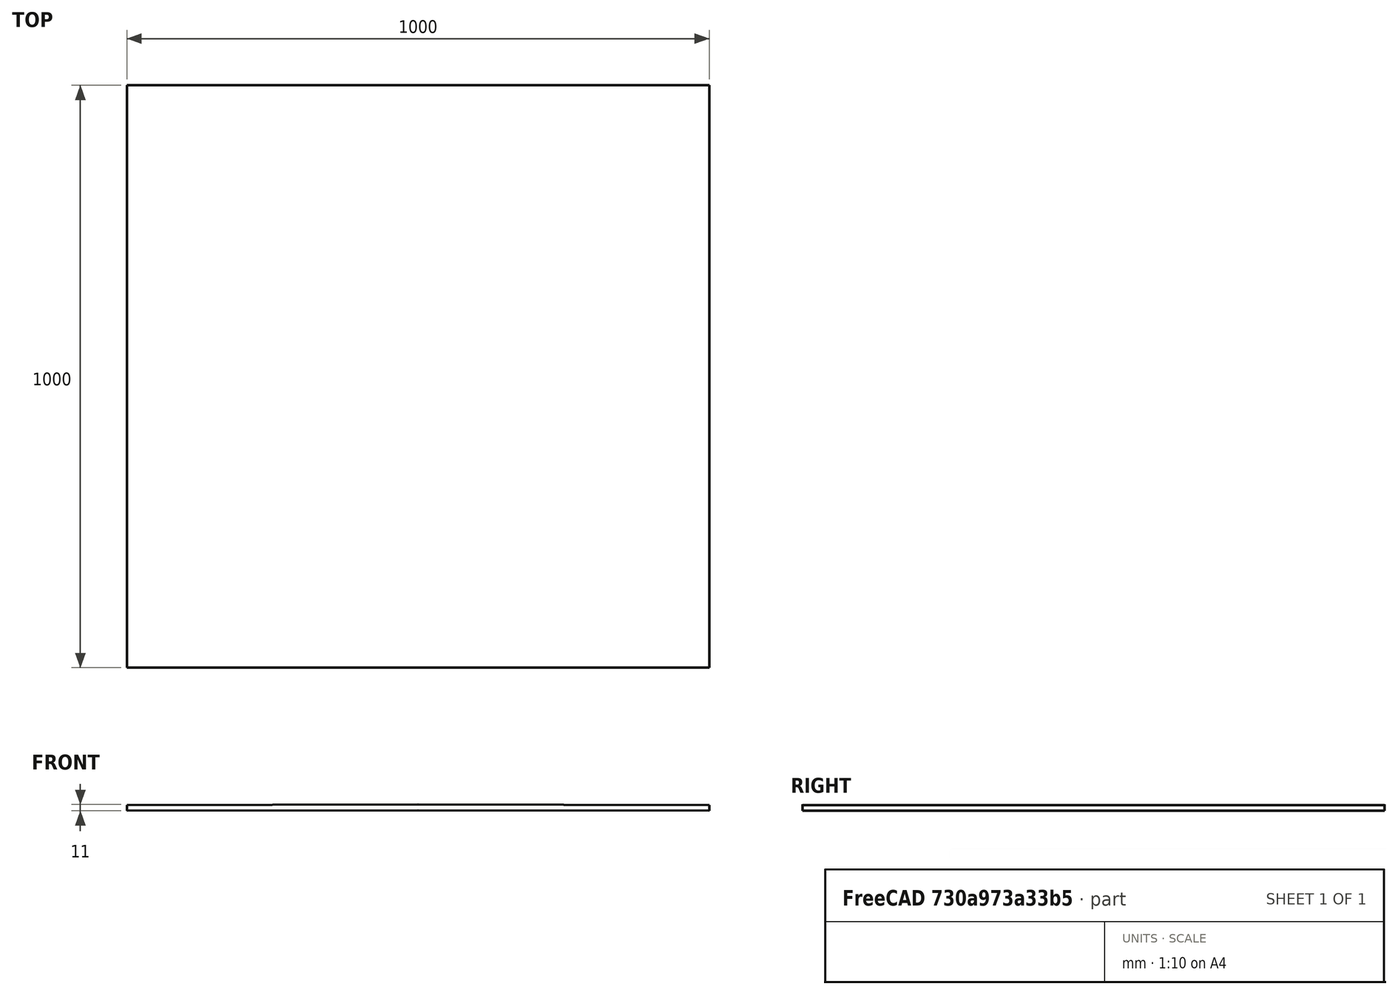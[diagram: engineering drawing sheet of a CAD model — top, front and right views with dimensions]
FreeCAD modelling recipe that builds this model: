
FCSTD DOCUMENT  (FreeCAD 0.21R33694 (Git))
Label: Elastica_3
License: All rights reserved
LicenseURL: http://en.wikipedia.org/wiki/All_rights_reserved
objects: Fem::ConstraintDisplacement×3, Sketcher::SketchObject×1, Part::Extrusion×1, App::MaterialObjectPython×1, Fem::ConstraintFixed×1, Fem::ConstraintForce×1, Fem::FemMeshObjectPython×1, Fem::FemSolverObjectPython×1, Fem::FemAnalysis×1
note: 2 computed .brp shape members not serialized (recipe doc carries the construction recipe); baked Part::Feature solids carry a one-line shape summary decoded from their .brp

FEATURE [Sketcher::SketchObject] Sketch
  FullyConstrained = true
  Placement = pos=(0,0,0) rot=(1,0,0;1.5708rad)
  sketch-geometry (6):
    g0: LineSegment StartX=0 StartY=0 StartZ=0 EndX=0 EndY=10 EndZ=0
    g1: LineSegment StartX=0 StartY=10 StartZ=0 EndX=500 EndY=11 EndZ=0
    g2: LineSegment StartX=500 StartY=11 StartZ=0 EndX=1000 EndY=10 EndZ=0
    g3: LineSegment StartX=1000 StartY=10 StartZ=0 EndX=1000 EndY=0 EndZ=0
    g4: LineSegment StartX=1000 StartY=0 StartZ=0 EndX=500 EndY=1 EndZ=0
    g5: LineSegment StartX=500 StartY=1 StartZ=0 EndX=0 EndY=-1e-16 EndZ=0
  constraints (17):
    c: Coincident(g-1,g0)
    c: PointOnObject(g0,g-2)
    c: Coincident(g0,g1)
    c: Coincident(g1,g2)
    c: Coincident(g2,g3)
    c: Vertical(g3)
    c: Coincident(g3,g4)
    c: Coincident(g4,g5)
    c: Coincident(g5,g0)
    c: DistanceY(g0,g0) = 10
    c: DistanceY(g3,g3) = 10
    c: DistanceY(g4,g1) = 10
    c: PointOnObject(g3,g-1)
    c: DistanceX(g0,g3) = 1000
    c: DistanceY(g0,g4) = 1
    c: DistanceX(g0,g4) = 500
    c: DistanceX(g0,g1) = 500
FEATURE [Part::Extrusion] Extrude
  Base = -> Sketch
  Dir = (0,-1,2e-16)
  DirMode = 2
  FaceMakerClass = Part::FaceMakerBullseye
  LengthFwd = 0
  LengthRev = 1000
  Solid = true
  Symmetric = false
FEATURE [App::MaterialObjectPython] MaterialSolid  # material (typed FeaturePython)
  Category = 0
  Material = AuthorAndLicense=(c) 2014 M. Münch - GNU Lesser General Public License (LGPL),CardName=Steel-St-E-315,Density=7800 kg/m^3,Father=Metal,+13 more (map truncated)
FEATURE [Fem::ConstraintFixed] ConstraintFixed
  NormalDirection = (-1,0,0)
  Normals = (15) [(-1,0,0),(-1,0,0),(-1,0,0),(-1,0,0),(-1,0,0),(-1,0,0),(-1,0,0),(-1,0,0),(-1,0,0),(-1,0,0),(-1,0,0),(-1,0,0),(-1,0,0),(-1,0,0),(-1,0,0)]
  Points = (15) [(0,0,-2.1e-15),(0,0,5),(0,0,10),(0,250,-5.71e-14),(0,250,5),(0,250,10),(0,500,-1.121e-13),(0,500,5),(0,500,10),(0,750,-1.671e-13),(0,750,5),+4 more]
  References = -> [Extrude]
FEATURE [Fem::ConstraintDisplacement] ConstraintDisplacement
  NormalDirection = (0,0,1)
  Normals = (4) [(0,0,1),(0,0,1),(0,0,1),(0,0,1)]
  Points = (4) [(1000,1000,-2.2204e-13),(1000,666.667,-1.48707e-13),(1000,333.333,-7.53733e-14),(1000,0,-2.04e-15)]
  References = -> [Extrude]
  Scale = 33
  hasXFormula = false
  hasYFormula = false
  hasZFormula = false
  rotxFix = false
  rotxFree = true
  rotyFix = false
  rotyFree = true
  rotzFix = false
  rotzFree = true
  useFlowSurfaceForce = false
  xDisplacement = 0
  xFix = false
  xFree = true
  xRotation = 0
  yDisplacement = 0
  yFix = false
  yFree = false
  yRotation = 0
  zDisplacement = 0
  zFix = false
  zFree = false
  zRotation = 0
FEATURE [Fem::ConstraintForce] ConstraintForce
  DirectionVector = (-1,0,0)
  Force = 1000000
  NormalDirection = (1,0,0)
  Points = (15) [(1000,0,10),(1000,0,5),(1000,0,-1.77636e-15),(1000,250,10),(1000,250,5),(1000,250,-5.68434e-14),(1000,500,10),(1000,500,5),(1000,500,-1.1191e-13),+6 more]
  References = -> [Extrude]
  Reversed = true
FEATURE [Fem::FemMeshObjectPython] FEMMeshGmsh  # FEM object (typed FeaturePython)
  Algorithm2D = 0
  Algorithm3D = 0
  CharacteristicLengthMax = 0
  CharacteristicLengthMin = 0
  CoherenceMesh = true
  ElementDimension = 0
  ElementOrder = 1
  GeometryTolerance = 1e-06
  GroupsOfNodes = false
  HighOrderOptimize = 0
  MeshSizeFromCurvature = 12
  OptimizeNetgen = false
  OptimizeStd = true
  Part = -> Extrude
  RecombinationAlgorithm = 0
  Recombine3DAll = false
  RecombineAll = false
  SecondOrderLinear = false
FEATURE [Fem::FemSolverObjectPython] SolverCcxTools  # FEM object (typed FeaturePython)
  AnalysisType = 0
  BeamShellResultOutput3D = false
  BucklingFactors = 1
  EigenmodeHighLimit = 1000000
  EigenmodeLowLimit = 0
  EigenmodesCount = 10
  GeometricalNonlinearity = 0
  IterationsControlParameterCutb = 0.25,0.5,0.75,0.85,,,1.5,
  IterationsControlParameterIter = 4,8,9,200,10,400,,200,,
  IterationsControlParameterTimeUse = false
  IterationsThermoMechMaximum = 2000
  IterationsUserDefinedIncrementations = false
  IterationsUserDefinedTimeStepLength = false
  MaterialNonlinearity = 0
  MatrixSolverType = 0
  SplitInputWriter = false
  ThermoMechSteadyState = true
  TimeEnd = 1
  TimeInitialStep = 0.01
FEATURE [Fem::ConstraintDisplacement] ConstraintDisplacement001
  NormalDirection = (0,1,0)
  Normals = (8) [(0,1,0),(0,1,0),(0,1,0),(0,1,0),(0,1,0),(0,1,0),(0,1,0),(0,1,0)]
  Points = (8) [(0,1000,-2.22045e-13),(0,1000,5.5),(250,1000,5.5),(500,1000,5.5),(500,1000,11),(750,1000,5.5),(1000,1000,-2.22045e-13),(1000,1000,5.5)]
  References = -> [Extrude]
  hasXFormula = false
  hasYFormula = false
  hasZFormula = false
  rotxFix = false
  rotxFree = true
  rotyFix = false
  rotyFree = true
  rotzFix = false
  rotzFree = true
  useFlowSurfaceForce = false
  xDisplacement = 0
  xFix = false
  xFree = true
  xRotation = 0
  yDisplacement = 0
  yFix = false
  yFree = false
  yRotation = 0
  zDisplacement = 0
  zFix = false
  zFree = true
  zRotation = 0
FEATURE [Fem::ConstraintDisplacement] ConstraintDisplacement002
  NormalDirection = (0,0,1)
  Normals = (16) [(0,0,1),(0,0,1),(0,0,1),(0,0,1),(0,0,1),(0,0,1),(0,0,1),(0,0,1),(0,0,1),(0,0,1),(0,0,1),(0,0,1),(0,0,1),(0,0,1),(0,0,1),(0,0,1)]
  Points = (16) [(1000,1000,-2.22e-13),(833.333,1000,0.333333),(666.667,1000,0.666667),(500,1000,1),(500,1000,1),(333.333,1000,0.666667),(166.667,1000,0.333333),+9 more]
  References = -> [Extrude]
  Scale = 24
  hasXFormula = false
  hasYFormula = false
  hasZFormula = false
  rotxFix = false
  rotxFree = true
  rotyFix = false
  rotyFree = true
  rotzFix = false
  rotzFree = true
  useFlowSurfaceForce = false
  xDisplacement = 0
  xFix = false
  xFree = true
  xRotation = 0
  yDisplacement = 0
  yFix = false
  yFree = true
  yRotation = 0
  zDisplacement = 0
  zFix = false
  zFree = false
  zRotation = 0
FEATURE [Fem::FemAnalysis] Analysis
  Group = -> [MaterialSolid,ConstraintFixed,ConstraintDisplacement,ConstraintForce,FEMMeshGmsh,SolverCcxTools,ConstraintDisplacement001,ConstraintDisplacement002]
